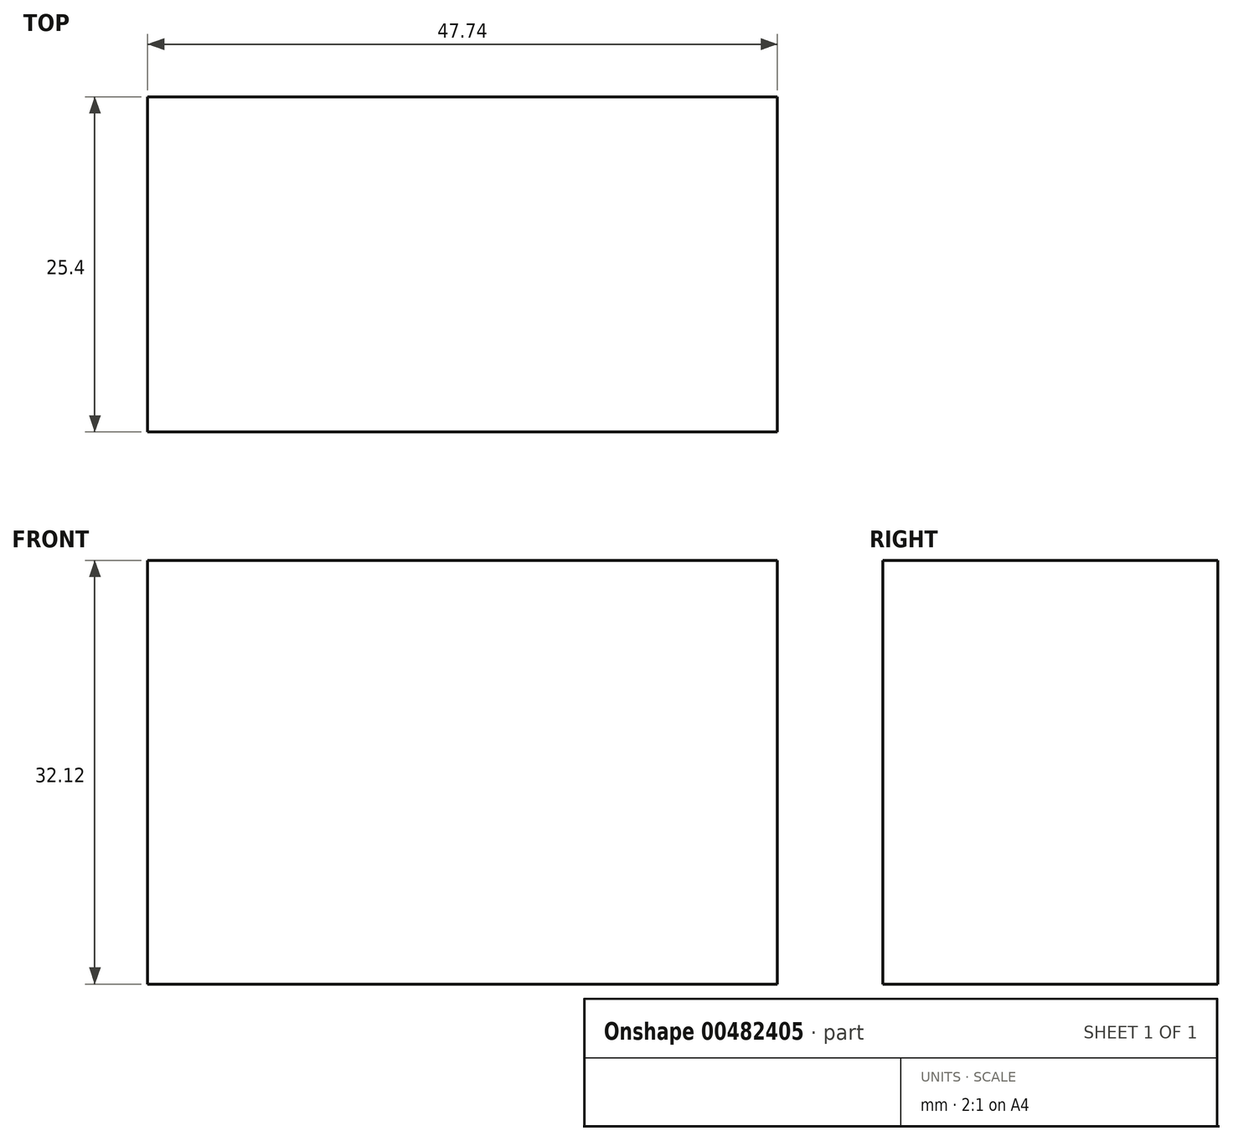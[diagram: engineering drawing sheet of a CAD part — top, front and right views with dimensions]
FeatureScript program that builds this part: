
annotation { "Feature Type Name" : "Feature", "Feature Type Description" : "" }
export const myFeature = defineFeature(function(context is Context, id is Id, definition is map)
    precondition{}
    {
        {
            var Q0;
            Q0=qCreatedBy(makeId("Front.planeOp"),FACE);
            var sketch = newSketch(context, id + "F0", { "sketchPlane" : qUnion([Q0])});
            skLineSegment(sketch, "E0", {"start": v(-61.92, 47.02) * mm, "end": v(-14.18, 47.02) * mm});
            skLineSegment(sketch, "E1", {"start": v(-14.18, 47.02) * mm, "end": v(-14.18, 14.9) * mm});
            skLineSegment(sketch, "E2", {"start": v(-14.18, 14.9) * mm, "end": v(-61.92, 14.9) * mm});
            skLineSegment(sketch, "E3", {"start": v(-61.92, 14.9) * mm, "end": v(-61.92, 47.02) * mm});
            skSolve(sketch);
        }
        {
            var Q0;
            Q0=makeQuery(id+"F0.imprint","IMPRINT",FACE,{"disambiguationData":[TD([[makeQuery(id+"F0.imprint","IMPRINT",EDGE,{"derivedFrom":sQuery(id+"F0.wireOp",EDGE,"E0")}),-1.0]])]});
            extrude(context, id + "F1", {"entities" : qUnion([Q0]), "depth" : 25.4 * mm});
        }
    });
